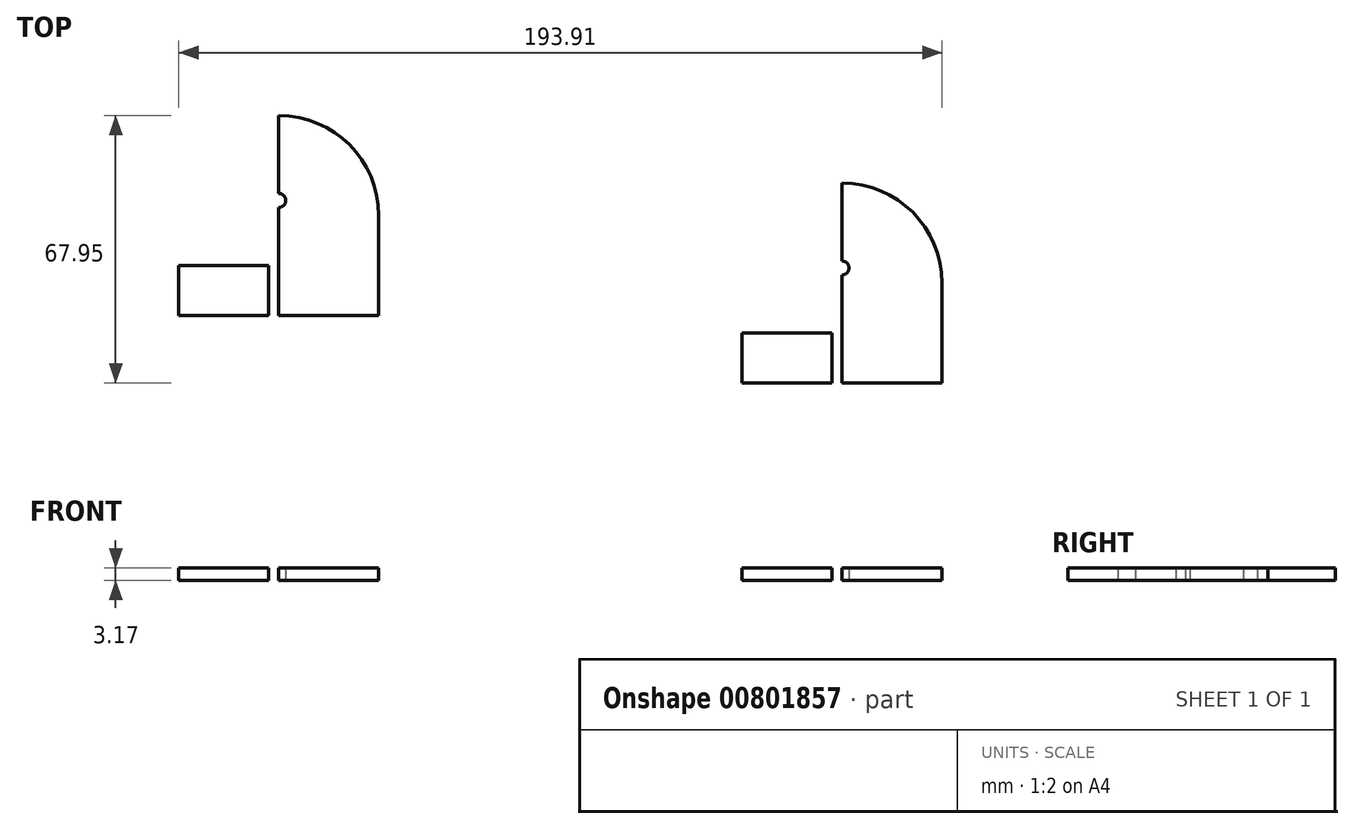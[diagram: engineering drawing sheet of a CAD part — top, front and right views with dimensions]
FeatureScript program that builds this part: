
annotation { "Feature Type Name" : "Feature", "Feature Type Description" : "" }
export const myFeature = defineFeature(function(context is Context, id is Id, definition is map)
    precondition{}
    {
        {
            var Q0;
            Q0=qCreatedBy(makeId("Top.planeOp"),FACE);
            var sketch = newSketch(context, id + "F0", { "sketchPlane" : qUnion([Q0])});
            skLineSegment(sketch, "E0", {"start": v(-134.13, 19.63) * mm, "end": v(-83.33, 19.63) * mm});
            skPoint(sketch, "E1", {"position": v(-108.73, 19.63) * mm});
            skLineSegment(sketch, "E2", {"start": v(-108.73, 19.63) * mm, "end": v(-108.73, 70.43) * mm});
            skLineSegment(sketch, "E3", {"start": v(-134.13, 45.03) * mm, "end": v(-134.13, 19.63) * mm});
            skLineSegment(sketch, "E4", {"start": v(-108.73, 70.43) * mm, "end": v(-108.73, 70.43) * mm});
            skPoint(sketch, "E5.visualSharp", {"position": v(-134.13, 70.43) * mm});
            skArc(sketch, "E5.filletArc", {"start": v(-108.73, 70.43) * mm, "mid": v(-126.7, 63) * mm, "end": v(-134.13, 45.03) * mm});
            skLineSegment(sketch, "E6", {"start": v(-83.33, 19.63) * mm, "end": v(-83.33, 45.03) * mm});
            skPoint(sketch, "E7.visualSharp", {"position": v(-83.33, 70.43) * mm});
            skArc(sketch, "E7.filletArc", {"start": v(-83.33, 45.03) * mm, "mid": v(-90.77, 63) * mm, "end": v(-108.73, 70.43) * mm});
            skPoint(sketch, "E8", {"position": v(-9.76, 2.42) * mm});
            skPoint(sketch, "E9", {"position": v(-108.73, 48.84) * mm});
            skCircle(sketch, "E10", {"center": v(-108.73, 48.84) * mm, "radius": 1.78 * mm});
            skLineSegment(sketch, "E11", {"start": v(-134.13, 19.63) * mm, "end": v(-134.13, 32.33) * mm});
            skLineSegment(sketch, "E12", {"start": v(-134.13, 32.33) * mm, "end": v(-111.27, 32.33) * mm});
            skLineSegment(sketch, "E13", {"start": v(-111.27, 32.33) * mm, "end": v(-111.27, 19.63) * mm});
            skLineSegment(sketch, "E14", {"start": v(8.98, 2.48) * mm, "end": v(59.78, 2.48) * mm});
            skPoint(sketch, "E15", {"position": v(34.38, 2.48) * mm});
            skLineSegment(sketch, "E16", {"start": v(34.38, 2.48) * mm, "end": v(34.38, 53.28) * mm});
            skLineSegment(sketch, "E17", {"start": v(8.98, 27.88) * mm, "end": v(8.98, 2.48) * mm});
            skLineSegment(sketch, "E18", {"start": v(34.38, 53.28) * mm, "end": v(34.38, 53.28) * mm});
            skPoint(sketch, "E19.visualSharp", {"position": v(8.98, 53.28) * mm});
            skArc(sketch, "E19.filletArc", {"start": v(34.38, 53.28) * mm, "mid": v(16.42, 45.84) * mm, "end": v(8.98, 27.88) * mm});
            skLineSegment(sketch, "E20", {"start": v(59.78, 2.48) * mm, "end": v(59.78, 27.88) * mm});
            skPoint(sketch, "E21.visualSharp", {"position": v(59.78, 53.28) * mm});
            skArc(sketch, "E21.filletArc", {"start": v(59.78, 27.88) * mm, "mid": v(52.34, 45.84) * mm, "end": v(34.38, 53.28) * mm});
            skPoint(sketch, "E22", {"position": v(133.35, -14.74) * mm});
            skPoint(sketch, "E23", {"position": v(34.38, 31.69) * mm});
            skCircle(sketch, "E24", {"center": v(34.38, 31.69) * mm, "radius": 1.78 * mm});
            skLineSegment(sketch, "E25", {"start": v(8.98, 2.48) * mm, "end": v(8.98, 15.18) * mm});
            skLineSegment(sketch, "E26", {"start": v(8.98, 15.18) * mm, "end": v(31.84, 15.18) * mm});
            skLineSegment(sketch, "E27", {"start": v(31.84, 15.18) * mm, "end": v(31.84, 2.48) * mm});
            skSolve(sketch);
        }
        {
            var Q0;
            {var subQ4=sQuery(id+"F0.wireOp",EDGE,"E6");Q0=makeQuery(id+"F0.imprint","IMPRINT",FACE,{"disambiguationData":[TD([[makeQuery(id+"F0.imprint","IMPRINT",EDGE,{"derivedFrom":subQ4}),1.0]])]});}
            var Q1;
            Q1=makeQuery(id+"F0.imprint","IMPRINT",FACE,{"disambiguationData":[TD([[makeQuery(id+"F0.imprint","IMPRINT",EDGE,{"derivedFrom":sQuery(id+"F0.wireOp",EDGE,"E3")}),1.0]])]});
            extrude(context, id + "F1", {"entities" : qUnion([Q0, Q1]), "depth" : 3.17 * mm, "offsetDistance" : 25.4 * mm});
        }
        {
            var Q0;
            {var subQ4=sQuery(id+"F0.wireOp",EDGE,"E20");Q0=makeQuery(id+"F0.imprint","IMPRINT",FACE,{"disambiguationData":[TD([[makeQuery(id+"F0.imprint","IMPRINT",EDGE,{"derivedFrom":subQ4}),1.0]])]});}
            var Q1;
            Q1=makeQuery(id+"F0.imprint","IMPRINT",FACE,{"disambiguationData":[TD([[makeQuery(id+"F0.imprint","IMPRINT",EDGE,{"derivedFrom":sQuery(id+"F0.wireOp",EDGE,"E17")}),1.0]])]});
            extrude(context, id + "F2", {"entities" : qUnion([Q0, Q1]), "depth" : 3.17 * mm, "offsetDistance" : 25.4 * mm});
        }
    });
